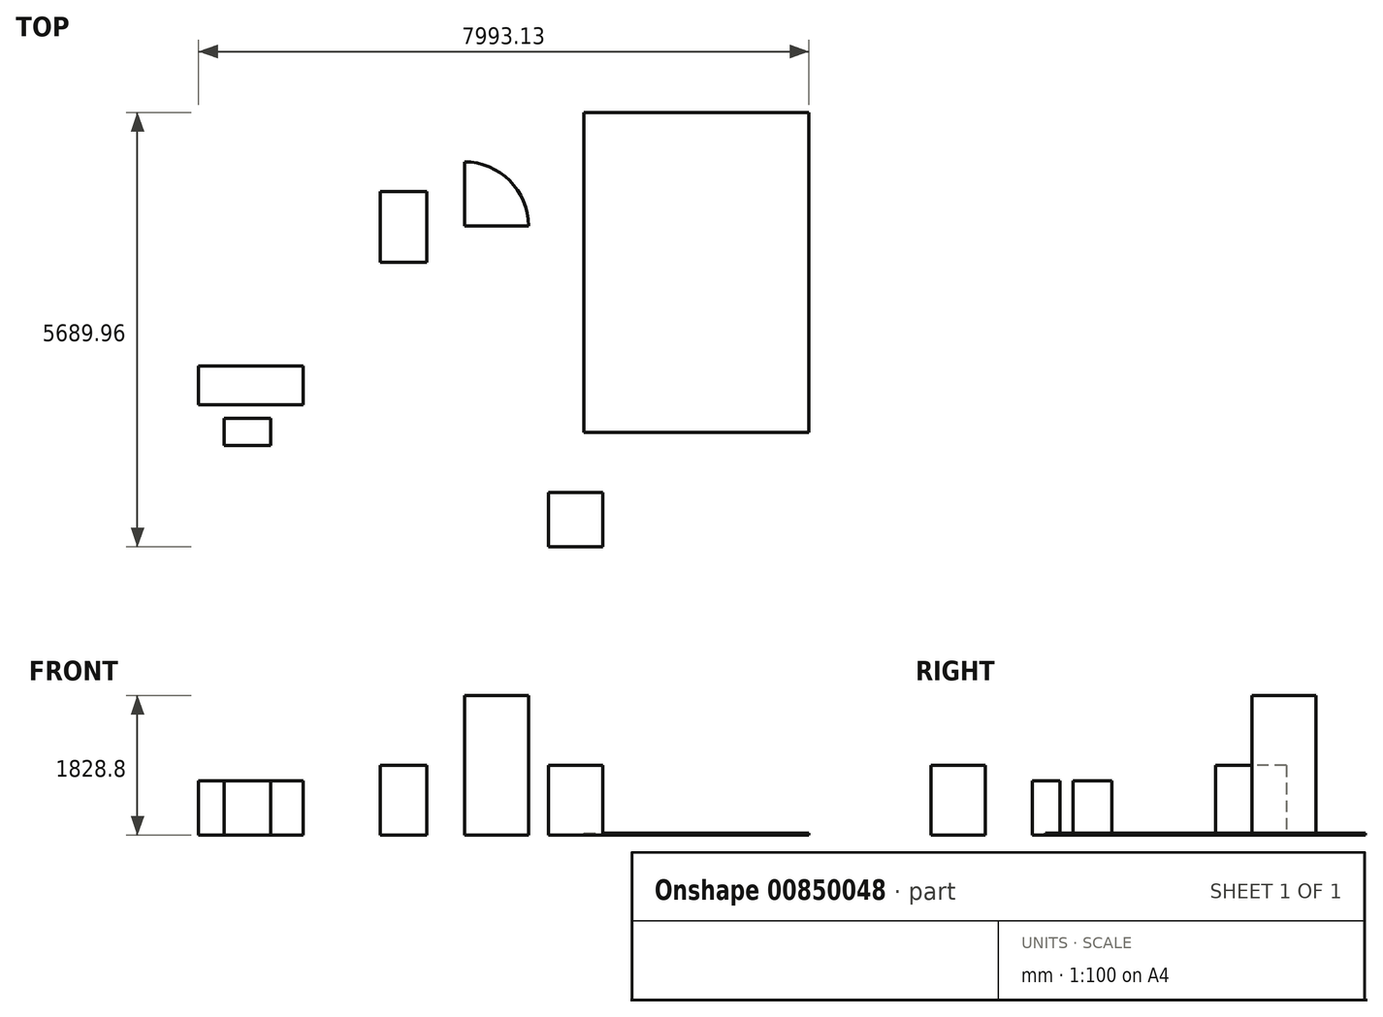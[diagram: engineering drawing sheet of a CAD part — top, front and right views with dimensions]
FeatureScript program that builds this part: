
annotation { "Feature Type Name" : "Feature", "Feature Type Description" : "" }
export const myFeature = defineFeature(function(context is Context, id is Id, definition is map)
    precondition{}
    {
        {
            var Q0;
            Q0=qCreatedBy(makeId("Top.planeOp"),FACE);
            var sketch = newSketch(context, id + "F0", { "sketchPlane" : qUnion([Q0])});
            skLineSegment(sketch, "E0.bottom", {"start": v(0, 0) * mm, "end": v(2946.4, 0) * mm});
            skLineSegment(sketch, "E0.top", {"start": v(0, 4191) * mm, "end": v(2946.4, 4191) * mm});
            skLineSegment(sketch, "E0.left", {"start": v(0, 0) * mm, "end": v(0, 4191) * mm});
            skLineSegment(sketch, "E0.right", {"start": v(2946.4, 0) * mm, "end": v(2946.4, 4191) * mm});
            skSolve(sketch);
        }
        {
            var Q0;
            Q0=qCreatedBy(makeId("Top.planeOp"),FACE);
            var sketch = newSketch(context, id + "F1", { "sketchPlane" : qUnion([Q0])});
            skLineSegment(sketch, "E1.bottom", {"start": v(-1312.43, 1224.9) * mm, "end": v(-804.43, 1224.9) * mm});
            skLineSegment(sketch, "E1.top", {"start": v(-1312.43, -146.7) * mm, "end": v(-804.43, -146.7) * mm});
            skLineSegment(sketch, "E1.left", {"start": v(-1312.43, 1224.9) * mm, "end": v(-1312.43, -146.7) * mm});
            skLineSegment(sketch, "E1.right", {"start": v(-804.43, 1224.9) * mm, "end": v(-804.43, -146.7) * mm});
            skSolve(sketch);
        }
        {
            var Q0;
            Q0=qCreatedBy(makeId("Top.planeOp"),FACE);
            var sketch = newSketch(context, id + "F2", { "sketchPlane" : qUnion([Q0])});
            skLineSegment(sketch, "E2.bottom", {"start": v(-627.07, 797.32) * mm, "end": v(-271.47, 797.32) * mm});
            skLineSegment(sketch, "E2.top", {"start": v(-627.07, 187.72) * mm, "end": v(-271.47, 187.72) * mm});
            skLineSegment(sketch, "E2.left", {"start": v(-627.07, 797.32) * mm, "end": v(-627.07, 187.72) * mm});
            skLineSegment(sketch, "E2.right", {"start": v(-271.47, 797.32) * mm, "end": v(-271.47, 187.72) * mm});
            skSolve(sketch);
        }
        {
            var Q0;
            Q0=makeQuery(id+"F0.imprint","IMPRINT",FACE,{"disambiguationData":[TD([[makeQuery(id+"F0.imprint","IMPRINT",EDGE,{"derivedFrom":sQuery(id+"F0.wireOp",EDGE,"E0.bottom")}),1.0]])]});
            extrude(context, id + "F3", {"entities" : qUnion([Q0]), "depth" : 25.4 * mm, "offsetDistance" : 25.4 * mm});
        }
        {
            var Q0;
            Q0=makeQuery(id+"F1.imprint","IMPRINT",FACE,{"disambiguationData":[TD([[makeQuery(id+"F1.imprint","IMPRINT",EDGE,{"derivedFrom":sQuery(id+"F1.wireOp",EDGE,"E1.bottom")}),-1.0]])]});
            extrude(context, id + "F4", {"entities" : qUnion([Q0]), "depth" : 711.2 * mm, "offsetDistance" : 25.4 * mm});
        }
        {
            var Q0;
            Q0=makeQuery(id+"F2.imprint","IMPRINT",FACE,{"disambiguationData":[TD([[makeQuery(id+"F2.imprint","IMPRINT",EDGE,{"derivedFrom":sQuery(id+"F2.wireOp",EDGE,"E2.bottom")}),-1.0]])]});
            extrude(context, id + "F5", {"entities" : qUnion([Q0]), "depth" : 711.2 * mm, "offsetDistance" : 25.4 * mm});
        }
        {
            var Q0;
            Q0=qCreatedBy(makeId("Top.planeOp"),FACE);
            var sketch = newSketch(context, id + "F6", { "sketchPlane" : qUnion([Q0])});
            skLineSegment(sketch, "E3.bottom", {"start": v(-464.27, -787.76) * mm, "end": v(246.93, -787.76) * mm});
            skLineSegment(sketch, "E3.top", {"start": v(-464.27, -1498.96) * mm, "end": v(246.93, -1498.96) * mm});
            skLineSegment(sketch, "E3.left", {"start": v(-464.27, -787.76) * mm, "end": v(-464.27, -1498.96) * mm});
            skLineSegment(sketch, "E3.right", {"start": v(246.93, -787.76) * mm, "end": v(246.93, -1498.96) * mm});
            skSolve(sketch);
        }
        {
            var Q0;
            Q0=makeQuery(id+"F6.imprint","IMPRINT",FACE,{"disambiguationData":[TD([[makeQuery(id+"F6.imprint","IMPRINT",EDGE,{"derivedFrom":sQuery(id+"F6.wireOp",EDGE,"E3.bottom")}),-1.0]])]});
            extrude(context, id + "F7", {"entities" : qUnion([Q0]), "depth" : 914.4 * mm, "offsetDistance" : 25.4 * mm});
        }
        {
            var Q0;
            Q0=qCreatedBy(makeId("Top.planeOp"),FACE);
            var sketch = newSketch(context, id + "F8", { "sketchPlane" : qUnion([Q0])});
            skLineSegment(sketch, "E4", {"start": v(-1565.33, 3544.33) * mm, "end": v(-1565.33, 2705.81) * mm});
            skLineSegment(sketch, "E5", {"start": v(-1565.33, 2705.81) * mm, "end": v(-726.82, 2705.81) * mm});
            skArc(sketch, "E6", {"start": v(-726.82, 2705.81) * mm, "mid": v(-972.46, 3298.7) * mm, "end": v(-1565.33, 3544.33) * mm});
            skSolve(sketch);
        }
        {
            var Q0;
            Q0=makeQuery(id+"F8.imprint","IMPRINT",FACE,{"disambiguationData":[TD([[makeQuery(id+"F8.imprint","IMPRINT",EDGE,{"derivedFrom":sQuery(id+"F8.wireOp",EDGE,"E4")}),1.0]])]});
            extrude(context, id + "F9", {"entities" : qUnion([Q0]), "depth" : 1828.8 * mm, "offsetDistance" : 25.4 * mm});
        }
        {
            var Q0;
            Q0=qCreatedBy(makeId("Top.planeOp"),FACE);
            var sketch = newSketch(context, id + "F10", { "sketchPlane" : qUnion([Q0])});
            skLineSegment(sketch, "E7.bottom", {"start": v(-2670.13, 3153.4) * mm, "end": v(-2058.24, 3153.4) * mm});
            skLineSegment(sketch, "E7.top", {"start": v(-2670.13, 2229.9) * mm, "end": v(-2058.24, 2229.9) * mm});
            skLineSegment(sketch, "E7.left", {"start": v(-2670.13, 3153.4) * mm, "end": v(-2670.13, 2229.9) * mm});
            skLineSegment(sketch, "E7.right", {"start": v(-2058.24, 3153.4) * mm, "end": v(-2058.24, 2229.9) * mm});
            skSolve(sketch);
        }
        {
            var Q0;
            Q0=makeQuery(id+"F10.imprint","IMPRINT",FACE,{"disambiguationData":[TD([[makeQuery(id+"F10.imprint","IMPRINT",EDGE,{"derivedFrom":sQuery(id+"F10.wireOp",EDGE,"E7.bottom")}),-1.0]])]});
            extrude(context, id + "F11", {"entities" : qUnion([Q0]), "depth" : 914.4 * mm, "offsetDistance" : 25.4 * mm});
        }
        {
            var Q0;
            Q0=makeQuery(id+"F4.opExtrude","SWEPT_BODY",BODY,{"disambiguationData":[OSD([sQuery(id+"F1.wireOp",EDGE,"E1.bottom"),sQuery(id+"F1.wireOp",EDGE,"E1.top"),sQuery(id+"F1.wireOp",EDGE,"E1.left"),sQuery(id+"F1.wireOp",EDGE,"E1.right")])]});
            var Q1;
            Q1=makeQuery(id+"F5.opExtrude","SWEPT_BODY",BODY,{"disambiguationData":[OSD([sQuery(id+"F2.wireOp",EDGE,"E2.bottom"),sQuery(id+"F2.wireOp",EDGE,"E2.top"),sQuery(id+"F2.wireOp",EDGE,"E2.left"),sQuery(id+"F2.wireOp",EDGE,"E2.right")])]});
            var Q2;
            Q2=makeQuery(id+"F11.opExtrude","SWEPT_EDGE",EDGE,{"disambiguationData":[OSD([sQuery(id+"F10.wireOp",EDGE,"E7.top"),sQuery(id+"F10.wireOp",EDGE,"E7.left")])]});
            transform(context, id + "F12", {"entities" : qUnion([Q0, Q1]), "transformType" : TransformType.ROTATION, "transformAxis" : qUnion([Q2]), "angle" : 90 * degree, "makeCopy" : false});
        }
    });
